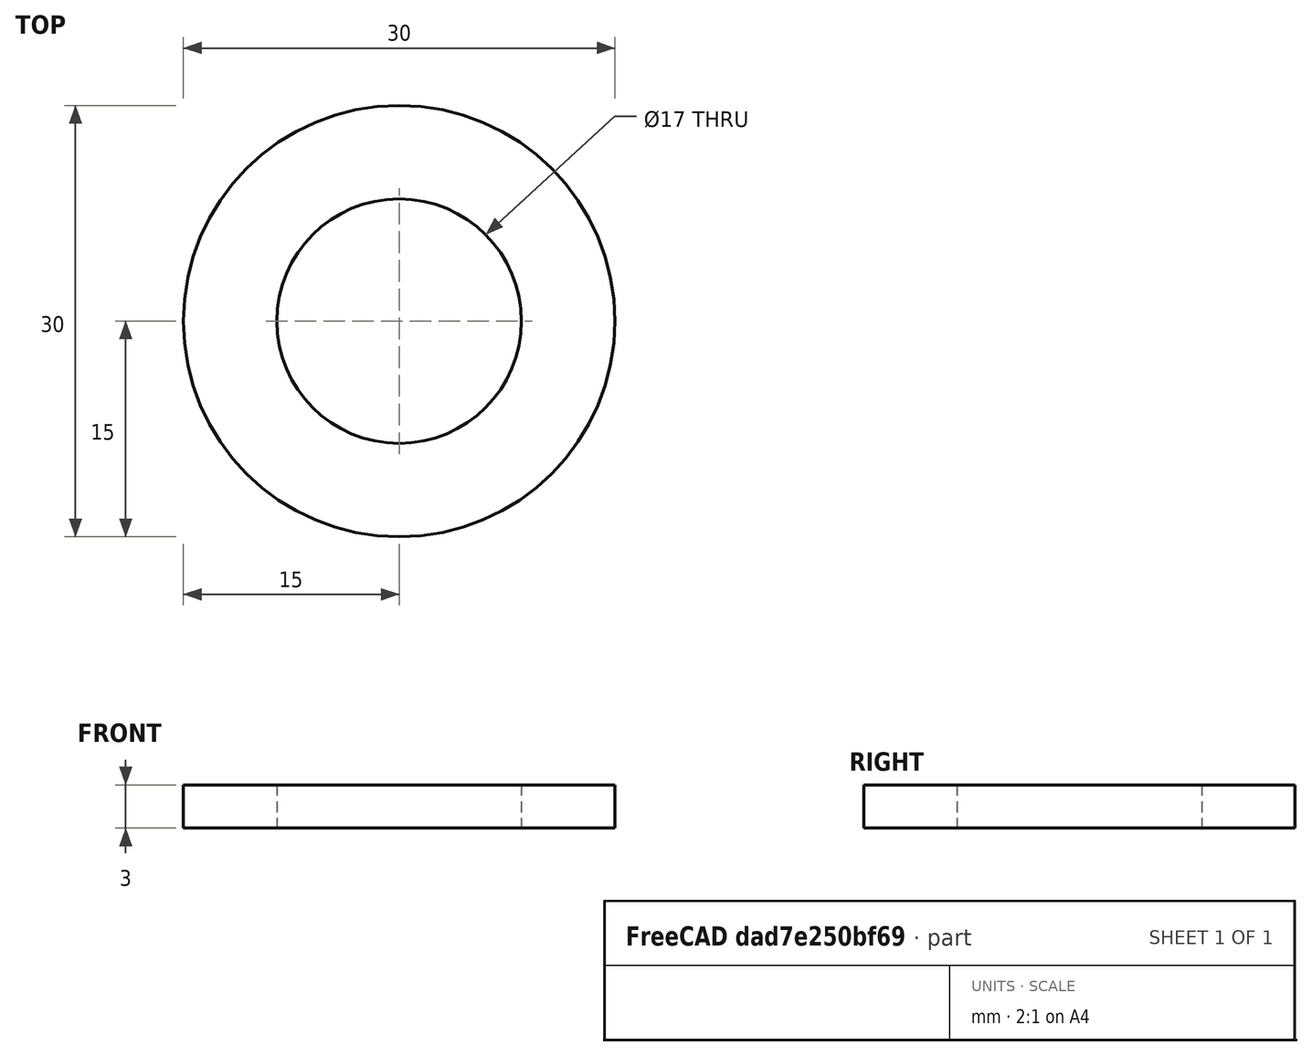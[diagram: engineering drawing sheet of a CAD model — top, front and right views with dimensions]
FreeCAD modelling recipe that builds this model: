
FCSTD DOCUMENT  (FreeCAD 0.14R3700 (Git))
Label: Scheibe DIN 125 - A 17
License: CC-BY 3.0
LicenseURL: http://creativecommons.org/licenses/by/3.0/
objects: Sketcher::SketchObject×1, PartDesign::Revolution×1, Part::Feature×1
note: 4 computed .brp shape members not serialized (recipe doc carries the construction recipe); baked Part::Feature solids carry a one-line shape summary decoded from their .brp

FEATURE [Sketcher::SketchObject] Sketch
  Placement = pos=(0,0,0) rot=(0.57735,0.57735,0.57735;2.0944rad)
  sketch-geometry (4):
    g0: LineSegment StartX=8.5 StartY=0 StartZ=0 EndX=15 EndY=0 EndZ=0
    g1: LineSegment StartX=15 StartY=0 StartZ=0 EndX=15 EndY=3 EndZ=0
    g2: LineSegment StartX=15 StartY=3 StartZ=0 EndX=8.5 EndY=3 EndZ=0
    g3: LineSegment StartX=8.5 StartY=3 StartZ=0 EndX=8.5 EndY=0 EndZ=0
  constraints (12):
    c: Coincident(g0,g1)
    c: Coincident(g1,g2)
    c: Coincident(g2,g3)
    c: Coincident(g3,g0)
    c: Horizontal(g0)
    c: Horizontal(g2)
    c: Vertical(g1)
    c: Vertical(g3)
    c: PointOnObject(g0,g-1)
    c: DistanceY(g1) = 3
    c: DistanceX(g-1,g2) = 8.5
    c: DistanceX(g-1,g1) = 15
FEATURE [PartDesign::Revolution] Revolution  label="Scheibe DIN 125 - A 17 #"
  Angle = 360
  Axis = (0,0,1)
  Base = (0,0,0)
  Placement = pos=(0,0,0) rot=(0.57735,0.57735,0.57735;2.0944rad)
  ReferenceAxis = -> Sketch [V_Axis]
  Reversed = true
  Sketch = -> Sketch
FEATURE [Part::Feature] Revolution001  label="Scheibe DIN 125 - A 17 #001"
  Placement = pos=(0,0,0) rot=(0.57735,0.57735,0.57735;2.0944rad)
  shape: bbox 30 x 30 x 3 mm, 4 faces (baked)
